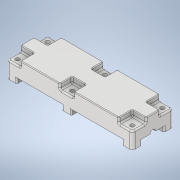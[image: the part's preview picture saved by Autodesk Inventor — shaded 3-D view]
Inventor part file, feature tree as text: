
AUTODESK INVENTOR PART (.ipt)
format: ipt  version: 2021 (Build 250183000, 183)  size: 845,312 bytes
history: native  units: mm
features: sketch x21, extrude x20, projected_geometry x9, fillet x3, other x1, mirror x1, boolean_combine x1
ambient origin geometry x8: Origin, YZ Plane, XZ Plane, XY Plane, X Axis, Y Axis, Z Axis, Center Point
bodies: Volumenkörper1 (feature_tree), Solid2 (feature_tree), Solid3 (feature_tree)
feature tree (56):
  extrude  "Extrusion1"  Depth=11.0mm
  other  "Spirale1"
  mirror  "Spiegeln1"
  extrude  "Extrusion5"  Depth=10.0mm
  extrude  "Extrusion6"  Depth=1.0mm
  boolean_combine  "Combine1"
  extrude  "Extrusion7"  Depth=10.0mm TaperAngle=0.0deg
  extrude  "Extrusion8"  Depth=100.0mm TaperAngle=0.0deg
  extrude  "Extrusion9"  Depth=24.0mm
  extrude  "Extrusion10"  Depth=12.0mm TaperAngle=0.0deg
  extrude  "Extrusion11"  Depth=4.0mm
  extrude  "Extrusion13"  Depth=10.0mm
  fillet  "Fillet2"  Radius=10.0mm
  fillet  "Fillet3"  Radius=77.15mm
  fillet  "Fillet4"  Radius=30.0mm
  extrude  "Extrusion14"  Depth=6.0mm
  extrude  "Extrusion15"  Depth=10.0mm TaperAngle=0.0deg
  extrude  "Extrusion16"  Depth=3.0mm
  extrude  "Extrusion17"  Depth=48.0mm
  extrude  "Extrusion19"  Depth=46.0mm
  extrude  "Extrusion20"  Depth=6.9mm
  extrude  "Extrusion21"  Depth=7.0mm
  extrude  "Extrusion22"  Depth=3.5mm
  extrude  "Extrusion23"  Depth=10.0mm
  extrude  "Extrusion25"  Depth=10.0mm
  extrude  "Extrusion26"  Depth=10.0mm
  sketch  "Skizze1"  dims[d0=6.0mm d1=11.0mm]
  sketch  "Skizze3"  dims[d2=36.0mm d3=0.0mm]
  projected_geometry  "Projizierte Kontur2"
  sketch  "Sketch7"  dims[d8=7.0mm d9=24.5mm d10=10.0mm d11=0.0mm d12=90.0deg d13=90.0deg d14=0.0mm d15=0.0mm d16=4.0mm]
  sketch  "Sketch8"  dims[d17=13.962634mm d18=1.0mm]
  sketch  "Sketch9"  dims[d19=0.1mm d32=10.0mm d33=0.0mm]
  projected_geometry  "Projected Loop4"
  sketch  "Sketch10"  dims[d34=7.0mm d35=100.0mm d36=0.0mm]
  sketch  "Sketch11"  dims[d37=82.0mm d38=0.0mm d39=24.0mm]
  projected_geometry  "Projected Loop5"
  projected_geometry  "Projected Loop6"
  sketch  "Sketch12"  dims[d40=30.0mm d41=12.0mm d42=0.0mm]
  sketch  "Sketch13"  dims[d43=3.0mm d44=4.0mm]
  projected_geometry  "Projected Loop7"
  projected_geometry  "Projected Loop8"
  sketch  "Sketch15"  dims[d45=4.0mm d46=20.0mm d48=22.0mm d49=20.0mm d51=84.0mm d54=10.0mm d55=0.0mm d56=77.15mm d57=30.0mm]
  sketch  "Sketch16"  dims[d62=4.0mm d63=0.0mm d64=6.0mm]
  projected_geometry  "Projected Loop10"
  sketch  "Sketch17"  dims[d65=10.0mm d66=0.0mm d67=10.0mm d68=0.0mm]
  projected_geometry  "Projected Loop11"
  projected_geometry  "Projected Loop12"
  sketch  "Sketch18"  dims[d76=3.0mm d77=3.0mm]
  sketch  "Sketch19"  dims[d78=4.0mm d79=48.0mm]
  sketch  "Sketch21"  dims[d80=46.0mm d81=4.0mm]
  sketch  "Sketch22"  dims[d85=7.0mm d86=6.9mm]
  sketch  "Sketch23"  dims[d87=3.5mm d88=7.0mm]
  sketch  "Sketch24"  dims[d89=6.9mm d90=3.5mm]
  sketch  "Sketch25"  dims[d91=10.0mm d92=10.0mm]
  sketch  "Sketch27"  dims[d93=10.0mm d94=10.0mm]
  sketch  "Sketch28"  dims[d95=10.0mm d96=10.0mm d97=10.0mm d98=10.0mm d99=10.0mm d100=10.0mm d101=10.0mm d102=10.0mm d103=4.0mm d104=0.0mm d105=1.0mm d106=1.0mm d107=2.0mm d108=0.5mm d109=6.5mm d110=2.1mm d111=0.0mm d112=6.5mm d113=2.1mm d114=0.0mm d115=180.0deg d116=6.9mm d117=6.9mm d118=6.9mm d119=6.9mm d120=12.0mm d121=0.2mm d122=0.0mm d123=15.0mm d124=0.2mm d125=0.0mm d126=7.9mm d127=0.0mm d128=7.9mm d129=0.0mm d132=1.9mm d133=0.0mm d134=5.1mm d135=5.0mm d136=0.0mm d137=6.6mm d138=1.9mm d139=0.0mm d140=4.1mm d141=3.1mm d142=0.0mm d143=6.6mm d144=3.1mm d145=0.0mm d149=6.6mm d150=0.2mm d151=0.0mm d152=5.1mm d153=7.9mm d154=0.0mm]
